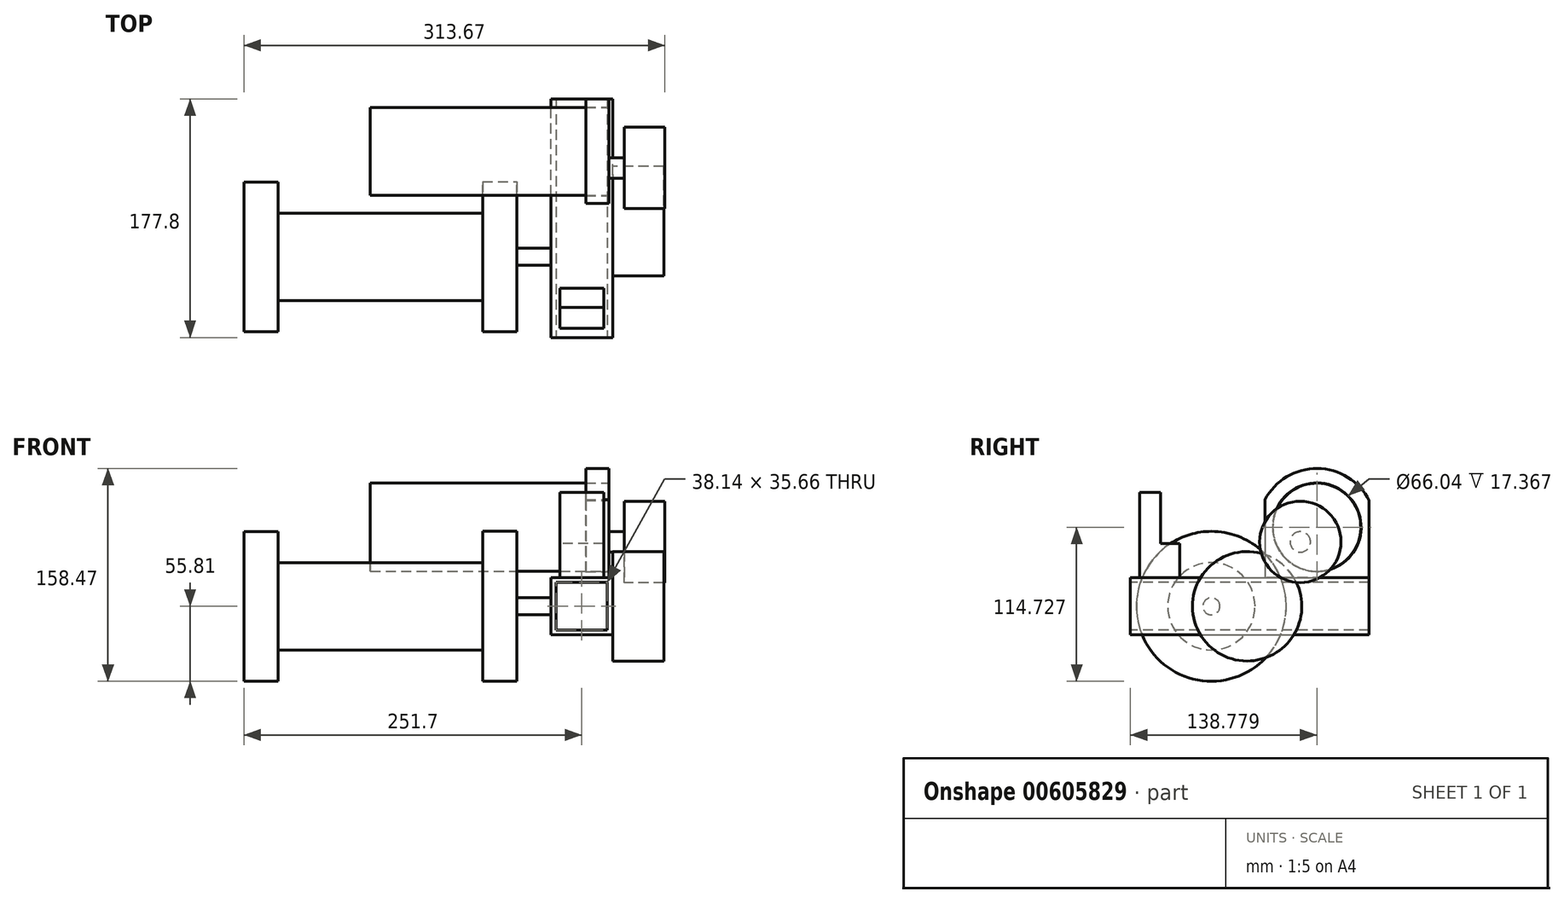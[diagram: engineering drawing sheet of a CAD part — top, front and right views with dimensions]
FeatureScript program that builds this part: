
annotation { "Feature Type Name" : "Feature", "Feature Type Description" : "" }
export const myFeature = defineFeature(function(context is Context, id is Id, definition is map)
    precondition{}
    {
        {
            var Q0;
            Q0=qCreatedBy(makeId("Front.planeOp"),FACE);
            var sketch = newSketch(context, id + "F0", { "sketchPlane" : qUnion([Q0])});
            skLineSegment(sketch, "E0.bottom", {"start": v(23.1, -21.24) * mm, "end": v(-23.1, -21.24) * mm});
            skLineSegment(sketch, "E0.top", {"start": v(23.1, 21.24) * mm, "end": v(-23.1, 21.24) * mm});
            skLineSegment(sketch, "E0.left", {"start": v(23.1, -21.24) * mm, "end": v(23.1, 21.24) * mm});
            skLineSegment(sketch, "E0.right", {"start": v(-23.1, -21.24) * mm, "end": v(-23.1, 21.24) * mm});
            skPoint(sketch, "E0.middle", {"position": v(0, 0) * mm});
            skSolve(sketch);
        }
        {
            var Q0;
            Q0 = qSketchRegion(id + "F0", true);
            extrude(context, id + "F1", {"entities" : qUnion([Q0]), "depth" : 177.8 * mm, "offsetDistance" : 25.4 * mm});
        }
        {
            var Q0;
            Q0=makeQuery(id+"F1.opExtrude","CAP_FACE",FACE,{"disambiguationData":[OSD([sQuery(id+"F0.wireOp",EDGE,"E0.bottom"),sQuery(id+"F0.wireOp",EDGE,"E0.top"),sQuery(id+"F0.wireOp",EDGE,"E0.left"),sQuery(id+"F0.wireOp",EDGE,"E0.right")])],"isStart":false});
            var sketch = newSketch(context, id + "F2", { "sketchPlane" : qUnion([Q0])});
            skLineSegment(sketch, "E1.bottom", {"start": v(19.07, -17.83) * mm, "end": v(-19.07, -17.83) * mm});
            skLineSegment(sketch, "E1.top", {"start": v(19.07, 17.83) * mm, "end": v(-19.07, 17.83) * mm});
            skLineSegment(sketch, "E1.left", {"start": v(19.07, -17.83) * mm, "end": v(19.07, 17.83) * mm});
            skLineSegment(sketch, "E1.right", {"start": v(-19.07, -17.83) * mm, "end": v(-19.07, 17.83) * mm});
            skPoint(sketch, "E1.middle", {"position": v(0, 0) * mm});
            skSolve(sketch);
        }
        {
            var Q0;
            Q0 = qSketchRegion(id + "F2", true);
            extrude(context, id + "F3", {"entities" : qUnion([Q0]), "operationType" : NewBodyOperationType.REMOVE, "oppositeDirection" : true, "depth" : 254 * mm, "offsetDistance" : 25.4 * mm});
        }
        {
            var Q0;
            Q0=makeQuery(id+"F1.opExtrude","SWEPT_FACE",FACE,{"disambiguationData":[OSD([sQuery(id+"F0.wireOp",EDGE,"E0.left")])]});
            var sketch = newSketch(context, id + "F4", { "sketchPlane" : qUnion([Q0])});
            skCircle(sketch, "E2", {"center": v(-90.96, 0) * mm, "radius": 40.77 * mm});
            skSolve(sketch);
        }
        {
            var Q0;
            Q0 = qSketchRegion(id + "F4", true);
            extrude(context, id + "F5", {"entities" : qUnion([Q0]), "operationType" : NewBodyOperationType.ADD, "depth" : 38.1 * mm, "offsetDistance" : 25.4 * mm});
        }
        {
            var Q0;
            Q0=makeQuery(id+"F1.opExtrude","SWEPT_FACE",FACE,{"disambiguationData":[OSD([sQuery(id+"F0.wireOp",EDGE,"E0.top")])]});
            var sketch = newSketch(context, id + "F6", { "sketchPlane" : qUnion([Q0])});
            skLineSegment(sketch, "E3.bottom", {"start": v(20.31, 0) * mm, "end": v(2.95, 0) * mm});
            skLineSegment(sketch, "E3.top", {"start": v(20.31, -77.72) * mm, "end": v(2.95, -77.72) * mm});
            skLineSegment(sketch, "E3.left", {"start": v(20.31, 0) * mm, "end": v(20.31, -77.72) * mm});
            skLineSegment(sketch, "E3.right", {"start": v(2.95, 0) * mm, "end": v(2.95, -77.72) * mm});
            skPoint(sketch, "E3.middle", {"position": v(11.63, -38.86) * mm});
            skSolve(sketch);
        }
        {
            var Q0;
            Q0 = qSketchRegion(id + "F6", true);
            extrude(context, id + "F7", {"entities" : qUnion([Q0]), "operationType" : NewBodyOperationType.ADD, "depth" : 101.6 * mm, "offsetDistance" : 25.4 * mm});
        }
        {
            var Q0;
            Q0=makeQuery(id+"F7.opExtrude","SWEPT_FACE",FACE,{"disambiguationData":[OSD([sQuery(id+"F6.wireOp",EDGE,"E3.left")])]});
            var sketch = newSketch(context, id + "F8", { "sketchPlane" : qUnion([Q0])});
            skArc(sketch, "E4", {"start": v(0, 78.68) * mm, "mid": v(-38.67, 102.65) * mm, "end": v(-77.72, 79.3) * mm});
            skLineSegment(sketch, "E5", {"start": v(-77.72, 79.3) * mm, "end": v(-77.72, 122.84) * mm});
            skLineSegment(sketch, "E6", {"start": v(-77.72, 122.84) * mm, "end": v(0, 122.84) * mm});
            skLineSegment(sketch, "E7", {"start": v(0, 122.84) * mm, "end": v(0, 78.68) * mm});
            skSolve(sketch);
        }
        {
            var Q0;
            Q0 = qSketchRegion(id + "F8", true);
            extrude(context, id + "F9", {"entities" : qUnion([Q0]), "operationType" : NewBodyOperationType.REMOVE, "oppositeDirection" : true, "depth" : 254 * mm, "offsetDistance" : 25.4 * mm});
        }
        {
            var Q0;
            Q0=makeQuery(id+"F7.opExtrude","SWEPT_FACE",FACE,{"disambiguationData":[OSD([sQuery(id+"F6.wireOp",EDGE,"E3.left")])]});
            var sketch = newSketch(context, id + "F10", { "sketchPlane" : qUnion([Q0])});
            skCircle(sketch, "E8", {"center": v(-39.02, 58.92) * mm, "radius": 33.02 * mm});
            skSolve(sketch);
        }
        {
            var Q0;
            Q0 = qSketchRegion(id + "F10", true);
            extrude(context, id + "F11", {"entities" : qUnion([Q0]), "operationType" : NewBodyOperationType.REMOVE, "oppositeDirection" : true, "depth" : 254 * mm, "offsetDistance" : 25.4 * mm});
        }
        {
            var Q0;
            Q0=makeQuery(id+"F1.opExtrude","SWEPT_FACE",FACE,{"disambiguationData":[OSD([sQuery(id+"F0.wireOp",EDGE,"E0.top")])]});
            var sketch = newSketch(context, id + "F12", { "sketchPlane" : qUnion([Q0])});
            skLineSegment(sketch, "E9.bottom", {"start": v(16.28, -170.97) * mm, "end": v(-16.28, -170.97) * mm});
            skLineSegment(sketch, "E9.top", {"start": v(16.28, -141) * mm, "end": v(-16.28, -141) * mm});
            skLineSegment(sketch, "E9.left", {"start": v(16.28, -170.97) * mm, "end": v(16.28, -141) * mm});
            skLineSegment(sketch, "E9.right", {"start": v(-16.28, -170.97) * mm, "end": v(-16.28, -141) * mm});
            skPoint(sketch, "E9.middle", {"position": v(0, -155.98) * mm});
            skSolve(sketch);
        }
        {
            var Q0;
            Q0 = qSketchRegion(id + "F12", true);
            extrude(context, id + "F13", {"entities" : qUnion([Q0]), "operationType" : NewBodyOperationType.ADD, "depth" : 25.4 * mm, "offsetDistance" : 25.4 * mm});
        }
        {
            var Q0;
            Q0=makeQuery(id+"F13.opExtrude","CAP_FACE",FACE,{"disambiguationData":[OSD([sQuery(id+"F12.wireOp",EDGE,"E9.bottom"),sQuery(id+"F12.wireOp",EDGE,"E9.top"),sQuery(id+"F12.wireOp",EDGE,"E9.left"),sQuery(id+"F12.wireOp",EDGE,"E9.right")])],"isStart":false});
            var sketch = newSketch(context, id + "F14", { "sketchPlane" : qUnion([Q0])});
            skLineSegment(sketch, "E10.bottom", {"start": v(16.28, -170.97) * mm, "end": v(-16.28, -170.97) * mm});
            skLineSegment(sketch, "E10.top", {"start": v(16.28, -155.46) * mm, "end": v(-16.28, -155.46) * mm});
            skLineSegment(sketch, "E10.left", {"start": v(16.28, -170.97) * mm, "end": v(16.28, -155.46) * mm});
            skLineSegment(sketch, "E10.right", {"start": v(-16.28, -170.97) * mm, "end": v(-16.28, -155.46) * mm});
            skPoint(sketch, "E10.middle", {"position": v(0, -163.22) * mm});
            skPoint(sketch, "E10.middle.positionSnap0", {"position": v(0, -170.97) * mm});
            skPoint(sketch, "E10.centerSnap0", {"position": v(0, -170.97) * mm});
            skSolve(sketch);
        }
        {
            var Q0;
            Q0 = qSketchRegion(id + "F14", true);
            extrude(context, id + "F15", {"entities" : qUnion([Q0]), "operationType" : NewBodyOperationType.ADD, "depth" : 38.1 * mm, "offsetDistance" : 25.4 * mm});
        }
        {
            var Q0;
            Q0=makeQuery(id+"F7.opExtrude","SWEPT_FACE",FACE,{"disambiguationData":[OSD([sQuery(id+"F6.wireOp",EDGE,"E3.left")])]});
            var sketch = newSketch(context, id + "F16", { "sketchPlane" : qUnion([Q0])});
            skCircle(sketch, "E11", {"center": v(-39.02, 58.92) * mm, "radius": 32.77 * mm});
            skSolve(sketch);
        }
        {
            var Q0;
            Q0 = qSketchRegion(id + "F16", true);
            extrude(context, id + "F17", {"entities" : qUnion([Q0]), "oppositeDirection" : true, "depth" : 177.8 * mm, "offsetDistance" : 25.4 * mm});
        }
        {
            var Q0;
            Q0=makeQuery(id+"F17.opExtrude","CAP_FACE",FACE,{"disambiguationData":[OSD([sQuery(id+"F16.wireOp",EDGE,"E11")])],"isStart":true});
            var sketch = newSketch(context, id + "F18", { "sketchPlane" : qUnion([Q0])});
            skCircle(sketch, "E12", {"center": v(-51.35, 47.98) * mm, "radius": 7.62 * mm});
            skSolve(sketch);
        }
        {
            var Q0;
            Q0 = qSketchRegion(id + "F18", true);
            extrude(context, id + "F19", {"entities" : qUnion([Q0]), "operationType" : NewBodyOperationType.ADD, "depth" : 11.18 * mm, "offsetDistance" : 25.4 * mm});
        }
        {
            var Q0;
            Q0=makeQuery(id+"F19.opExtrude","CAP_FACE",FACE,{"disambiguationData":[OSD([sQuery(id+"F18.wireOp",EDGE,"E12")])],"isStart":false});
            var sketch = newSketch(context, id + "F20", { "sketchPlane" : qUnion([Q0])});
            skCircle(sketch, "E13", {"center": v(-51.35, 47.98) * mm, "radius": 30.3 * mm});
            skSolve(sketch);
        }
        {
            var Q0;
            Q0 = qSketchRegion(id + "F20", true);
            extrude(context, id + "F21", {"entities" : qUnion([Q0]), "depth" : 30.48 * mm, "offsetDistance" : 25.4 * mm});
        }
        {
            var Q0;
            Q0=makeQuery(id+"F1.opExtrude","SWEPT_FACE",FACE,{"disambiguationData":[OSD([sQuery(id+"F0.wireOp",EDGE,"E0.right")])]});
            var sketch = newSketch(context, id + "F22", { "sketchPlane" : qUnion([Q0])});
            skCircle(sketch, "E14", {"center": v(117.58, 0) * mm, "radius": 6.35 * mm});
            skSolve(sketch);
        }
        {
            var Q0;
            Q0 = qSketchRegion(id + "F22", true);
            extrude(context, id + "F23", {"entities" : qUnion([Q0]), "operationType" : NewBodyOperationType.ADD, "depth" : 25.4 * mm, "offsetDistance" : 25.4 * mm});
        }
        {
            var Q0;
            Q0=makeQuery(id+"F23.opExtrude","CAP_FACE",FACE,{"disambiguationData":[OSD([sQuery(id+"F22.wireOp",EDGE,"E14")])],"isStart":false});
            var sketch = newSketch(context, id + "F24", { "sketchPlane" : qUnion([Q0])});
            skCircle(sketch, "E15", {"center": v(117.58, 0) * mm, "radius": 55.81 * mm});
            skSolve(sketch);
        }
        {
            var Q0;
            Q0 = qSketchRegion(id + "F24", true);
            extrude(context, id + "F25", {"entities" : qUnion([Q0]), "operationType" : NewBodyOperationType.ADD, "depth" : 25.4 * mm, "offsetDistance" : 25.4 * mm});
        }
        {
            var Q0;
            Q0=makeQuery(id+"F25.opExtrude","CAP_FACE",FACE,{"disambiguationData":[OSD([sQuery(id+"F24.wireOp",EDGE,"E15")])],"isStart":false});
            var sketch = newSketch(context, id + "F26", { "sketchPlane" : qUnion([Q0])});
            skCircle(sketch, "E16", {"center": v(117.58, 0) * mm, "radius": 32.53 * mm});
            skSolve(sketch);
        }
        {
            var Q0;
            Q0 = qSketchRegion(id + "F26", true);
            extrude(context, id + "F27", {"entities" : qUnion([Q0]), "operationType" : NewBodyOperationType.ADD, "depth" : 152.4 * mm, "offsetDistance" : 25.4 * mm});
        }
        {
            var Q0;
            Q0=makeQuery(id+"F27.opExtrude","CAP_FACE",FACE,{"disambiguationData":[OSD([sQuery(id+"F26.wireOp",EDGE,"E16")])],"isStart":false});
            var sketch = newSketch(context, id + "F28", { "sketchPlane" : qUnion([Q0])});
            skCircle(sketch, "E17", {"center": v(117.58, 0) * mm, "radius": 55.72 * mm});
            skSolve(sketch);
        }
        {
            var Q0;
            Q0 = qSketchRegion(id + "F28", true);
            extrude(context, id + "F29", {"entities" : qUnion([Q0]), "operationType" : NewBodyOperationType.ADD, "depth" : 25.4 * mm, "offsetDistance" : 25.4 * mm});
        }
    });
